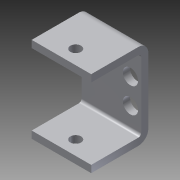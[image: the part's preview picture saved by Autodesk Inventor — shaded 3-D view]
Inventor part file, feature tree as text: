
AUTODESK INVENTOR PART (.ipt)
format: ipt  version: 2013 (Build 170138000, 138)  size: 144,896 bytes
history: native  units: in
note: dims shown in document units (in); Inventor stores cm internally (conversion verified against a paired STEP export)
features: sheet_metal_op x4, sketch x4, other x3, extrude x1
ambient origin geometry x8: Origin, YZ Plane, XZ Plane, XY Plane, X Axis, Y Axis, Z Axis, Center Point
bodies: Solid1 (feature_tree)
feature tree (12):
  sheet_metal_op  "Face1"
  sheet_metal_op  "Flange1"
  extrude  "Extrusion1"  Depth=1.15in
  sketch  "Sketch1"  dims[d4=0.5788in d5=1.15in]
  other  "Plate1"
  sketch  "Sketch2"  dims[d6=0.125in]
  other  "Plate2"
  sheet_metal_op  "Bend1"
  sheet_metal_op  "Corner1"
  sketch  "Sketch3"  dims[d7=0.125in]
  sketch  "Sketch9"  dims[d8=0.0625in d9=0.25in d10=0.125in d11=1.0in d12=90.0deg d13=0.05in d14=0.5in d15=0.125in d16=0.125in d17=0.25in d18=0.1875in d19=2999.0in d20=0.0in d21=0.575in d31=0.266in d33=0.266in d34=0.188in d35=0.125in d36=0.0in d37=0.316in d38=0.442in]
  other  "Cut4"
